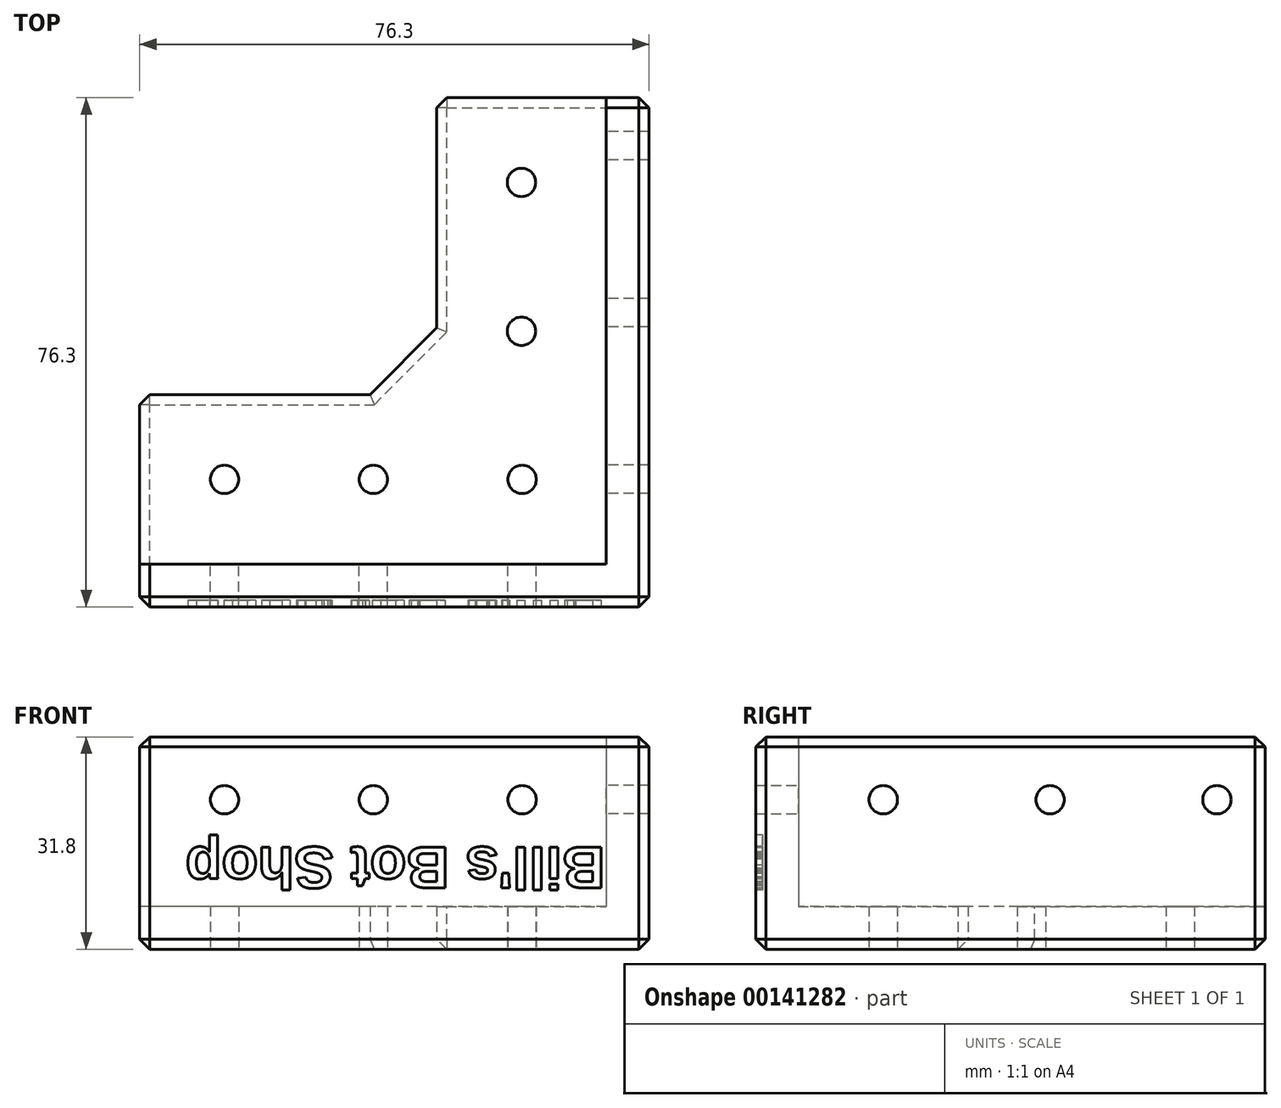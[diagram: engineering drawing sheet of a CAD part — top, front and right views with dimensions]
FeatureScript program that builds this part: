
annotation { "Feature Type Name" : "Feature", "Feature Type Description" : "" }
export const myFeature = defineFeature(function(context is Context, id is Id, definition is map)
    precondition{}
    {
        {
            var Q0;
            Q0=qCreatedBy(makeId("Top.planeOp"),FACE);
            var sketch = newSketch(context, id + "F0", { "sketchPlane" : qUnion([Q0])});
            skLineSegment(sketch, "E0.bottom", {"start": v(34.95, -12.7) * mm, "end": v(-34.95, -12.7) * mm});
            skLineSegment(sketch, "E0.top", {"start": v(34.95, 12.7) * mm, "end": v(28.55, 12.7) * mm, "construction": true});
            skLineSegment(sketch, "E0.left", {"start": v(34.95, -12.7) * mm, "end": v(34.95, 12.7) * mm});
            skLineSegment(sketch, "E0.right", {"start": v(-34.95, -12.7) * mm, "end": v(-34.95, 12.7) * mm});
            skPoint(sketch, "E0.middle", {"position": v(0, 0) * mm});
            skCircle(sketch, "E1", {"center": v(-22.25, 0) * mm, "radius": 2.12 * mm});
            skCircle(sketch, "E2.1.0.0", {"center": v(0.05, 0) * mm, "radius": 2.12 * mm});
            skCircle(sketch, "E2.2.0.0", {"center": v(22.35, 0) * mm, "radius": 2.12 * mm});
            skLineSegment(sketch, "E2.direction1", {"start": v(-22.25, 0) * mm, "end": v(0.05, 0) * mm, "construction": true});
            skLineSegment(sketch, "E3", {"start": v(28.55, 12.7) * mm, "end": v(28.55, -12.7) * mm, "construction": true});
            skLineSegment(sketch, "E4", {"start": v(9.55, 12.7) * mm, "end": v(9.55, 57.2) * mm});
            skLineSegment(sketch, "E5", {"start": v(9.55, 57.2) * mm, "end": v(34.95, 57.2) * mm});
            skLineSegment(sketch, "E6", {"start": v(34.95, 57.2) * mm, "end": v(34.95, 12.7) * mm});
            skCircle(sketch, "E7", {"center": v(22.25, 44.5) * mm, "radius": 2.12 * mm});
            skCircle(sketch, "E8", {"center": v(22.25, 22.2) * mm, "radius": 2.12 * mm});
            skLineSegment(sketch, "E9.trimOffspring", {"start": v(9.55, 12.7) * mm, "end": v(-34.95, 12.7) * mm});
            skSolve(sketch);
        }
        {
            var Q0;
            Q0=qSketchRegion(id+"F0",true);
            extrude(context, id + "F1", {"entities" : qUnion([Q0]), "depth" : 6.4 * mm});
        }
        {
            var Q0;
            Q0=makeQuery(id+"F1.opExtrude","SWEPT_FACE",FACE,{"disambiguationData":[OSD([sQuery(id+"F0.wireOp",EDGE,"E0.bottom")])]});
            var sketch = newSketch(context, id + "F2", { "sketchPlane" : qUnion([Q0])});
            skLineSegment(sketch, "E10.bottom", {"start": v(34.95, 0) * mm, "end": v(-34.95, 0) * mm});
            skLineSegment(sketch, "E10.top", {"start": v(34.95, 31.8) * mm, "end": v(-34.95, 31.8) * mm});
            skLineSegment(sketch, "E10.left", {"start": v(34.95, 0) * mm, "end": v(34.95, 31.8) * mm});
            skLineSegment(sketch, "E10.right", {"start": v(-34.95, 0) * mm, "end": v(-34.95, 31.8) * mm});
            skPoint(sketch, "E10.middle", {"position": v(0, 15.9) * mm});
            skCircle(sketch, "E11", {"center": v(-22.25, 22.4) * mm, "radius": 2.12 * mm});
            skCircle(sketch, "E12.1.0.0", {"center": v(0.05, 22.4) * mm, "radius": 2.12 * mm});
            skLineSegment(sketch, "E12.direction1", {"start": v(-22.25, 22.4) * mm, "end": v(0.05, 22.4) * mm, "construction": true});
            skLineSegment(sketch, "E13", {"start": v(28.55, 31.8) * mm, "end": v(28.55, 0) * mm, "construction": true});
            skCircle(sketch, "E14.0.2.0", {"center": v(22.35, 22.4) * mm, "radius": 2.12 * mm});
            skSolve(sketch);
        }
        {
            var Q0;
            Q0=qSketchRegion(id+"F2",true);
            extrude(context, id + "F3", {"entities" : qUnion([Q0]), "operationType" : NewBodyOperationType.ADD, "depth" : 6.4 * mm});
        }
        {
            var Q0;
            Q0=makeQuery(id+"F3.boolean.opBoolean","MERGE",FACE,{"derivedFrom":[makeQuery(id+"F1.opExtrude","SWEPT_FACE",FACE,{"disambiguationData":[OSD([sQuery(id+"F0.wireOp",EDGE,"E0.left")])]}),makeQuery(id+"F3.opExtrude","SWEPT_FACE",FACE,{"disambiguationData":[OSD([sQuery(id+"F2.wireOp",EDGE,"E10.left")])]})]});
            var sketch = newSketch(context, id + "F4", { "sketchPlane" : qUnion([Q0])});
            skLineSegment(sketch, "E15", {"start": v(-19.1, 31.8) * mm, "end": v(-19.1, 0) * mm});
            skLineSegment(sketch, "E16", {"start": v(-19.1, 0) * mm, "end": v(57.2, 0) * mm});
            skLineSegment(sketch, "E17", {"start": v(-12.7, 31.8) * mm, "end": v(-19.1, 31.8) * mm});
            skLineSegment(sketch, "E18", {"start": v(57.2, 0) * mm, "end": v(57.2, 31.8) * mm});
            skLineSegment(sketch, "E19", {"start": v(57.2, 31.8) * mm, "end": v(-12.7, 31.8) * mm});
            skCircle(sketch, "E20", {"center": v(0, 22.4) * mm, "radius": 2.12 * mm});
            skCircle(sketch, "E21.1.0.0", {"center": v(25, 22.4) * mm, "radius": 2.12 * mm});
            skCircle(sketch, "E21.2.0.0", {"center": v(50, 22.4) * mm, "radius": 2.12 * mm});
            skLineSegment(sketch, "E21.direction1", {"start": v(0, 22.4) * mm, "end": v(25, 22.4) * mm, "construction": true});
            skSolve(sketch);
        }
        {
            var Q0;
            Q0=qSketchRegion(id+"F4",true);
            extrude(context, id + "F5", {"entities" : qUnion([Q0]), "operationType" : NewBodyOperationType.ADD, "depth" : 6.4 * mm});
        }
        {
            var Q0;
            Q0=makeQuery(id+"F1.opExtrude","SWEPT_EDGE",EDGE,{"disambiguationData":[OSD([sQuery(id+"F0.wireOp",EDGE,"E4"),sQuery(id+"F0.wireOp",EDGE,"E9.trimOffspring")])]});
            chamfer(context, id + "F6", {"entities" : qUnion([Q0]), "width" : 10 * mm, "tangentPropagation" : true});
        }
        {
            var Q0;
            Q0=makeQuery(id+"F5.boolean.opBoolean","MERGE",EDGE,{"derivedFrom":[makeQuery(id+"F3.opExtrude","CAP_EDGE",EDGE,{"disambiguationData":[OSD([sQuery(id+"F2.wireOp",EDGE,"E10.bottom")])],"isStart":false}),makeQuery(id+"F5.opExtrude","SWEPT_EDGE",EDGE,{"disambiguationData":[OSD([sQuery(id+"F4.wireOp",EDGE,"E15"),sQuery(id+"F4.wireOp",EDGE,"E16")])]})]});
            var Q1;
            Q1=makeQuery(id+"F5.opExtrude","CAP_EDGE",EDGE,{"disambiguationData":[OSD([sQuery(id+"F4.wireOp",EDGE,"E16")])],"isStart":false});
            var Q2;
            Q2=makeQuery(id+"F5.opExtrude","CAP_EDGE",EDGE,{"disambiguationData":[OSD([sQuery(id+"F4.wireOp",EDGE,"E15")])],"isStart":false});
            var Q3;
            Q3=makeQuery(id+"F3.opExtrude","CAP_EDGE",EDGE,{"disambiguationData":[OSD([sQuery(id+"F2.wireOp",EDGE,"E10.right")])],"isStart":false});
            var Q4;
            Q4=makeQuery(id+"F3.boolean.opBoolean","MERGE",EDGE,{"derivedFrom":[makeQuery(id+"F1.opExtrude","CAP_EDGE",EDGE,{"disambiguationData":[OSD([sQuery(id+"F0.wireOp",EDGE,"E0.right")])],"isStart":true}),makeQuery(id+"F3.opExtrude","SWEPT_EDGE",EDGE,{"disambiguationData":[OSD([sQuery(id+"F2.wireOp",EDGE,"E10.bottom"),sQuery(id+"F2.wireOp",EDGE,"E10.right")])]})]});
            var Q5;
            Q5=makeQuery(id+"F1.opExtrude","CAP_EDGE",EDGE,{"disambiguationData":[OSD([sQuery(id+"F0.wireOp",EDGE,"E9.trimOffspring")])],"isStart":true});
            var Q6;
            Q6=makeQuery(id+"F1.opExtrude","CAP_EDGE",EDGE,{"disambiguationData":[OSD([sQuery(id+"F0.wireOp",EDGE,"E4")])],"isStart":true});
            var Q7;
            Q7=makeQuery(id+"F5.opExtrude","CAP_EDGE",EDGE,{"disambiguationData":[OSD([sQuery(id+"F4.wireOp",EDGE,"E18")])],"isStart":false});
            var Q8;
            Q8=makeQuery(id+"F5.boolean.opBoolean","MERGE",EDGE,{"derivedFrom":[makeQuery(id+"F1.opExtrude","CAP_EDGE",EDGE,{"disambiguationData":[OSD([sQuery(id+"F0.wireOp",EDGE,"E5")])],"isStart":true}),makeQuery(id+"F5.opExtrude","SWEPT_EDGE",EDGE,{"disambiguationData":[OSD([sQuery(id+"F4.wireOp",EDGE,"E16"),sQuery(id+"F4.wireOp",EDGE,"E18")])]})]});
            var Q9;
            {var subQ0=sQuery(id+"F0.wireOp",EDGE,"E9.trimOffspring");var subQ1=sQuery(id+"F0.wireOp",EDGE,"E4");Q9=makeQuery(id+"F6.opChamfer","BLEND_EDGE",EDGE,{"blendedFrom":[makeQuery(id+"F1.opExtrude","SWEPT_EDGE",EDGE,{"disambiguationData":[OSD([subQ1,subQ0])]}),makeQuery(id+"F5.boolean.opBoolean","MERGE",FACE,{"derivedFrom":[makeQuery(id+"F3.boolean.opBoolean","MERGE",FACE,{"derivedFrom":[makeQuery(id+"F1.opExtrude","CAP_FACE",FACE,{"disambiguationData":[OSD([sQuery(id+"F0.wireOp",EDGE,"E0.bottom"),sQuery(id+"F0.wireOp",EDGE,"E0.left"),sQuery(id+"F0.wireOp",EDGE,"E0.right"),sQuery(id+"F0.wireOp",EDGE,"E1"),sQuery(id+"F0.wireOp",EDGE,"E2.1.0.0"),sQuery(id+"F0.wireOp",EDGE,"E2.2.0.0"),subQ1,sQuery(id+"F0.wireOp",EDGE,"E5"),sQuery(id+"F0.wireOp",EDGE,"E6"),sQuery(id+"F0.wireOp",EDGE,"E7"),sQuery(id+"F0.wireOp",EDGE,"E8"),subQ0])],"isStart":true}),makeQuery(id+"F3.opExtrude","SWEPT_FACE",FACE,{"disambiguationData":[OSD([sQuery(id+"F2.wireOp",EDGE,"E10.bottom")])]})]}),makeQuery(id+"F5.opExtrude","SWEPT_FACE",FACE,{"disambiguationData":[OSD([sQuery(id+"F4.wireOp",EDGE,"E16")])]})]})],"blendedInto":[makeQuery(id+"F5.boolean.opBoolean","MERGE",FACE,{"derivedFrom":[makeQuery(id+"F3.boolean.opBoolean","MERGE",FACE,{"derivedFrom":[makeQuery(id+"F1.opExtrude","CAP_FACE",FACE,{"disambiguationData":[OSD([sQuery(id+"F0.wireOp",EDGE,"E0.bottom"),sQuery(id+"F0.wireOp",EDGE,"E0.left"),sQuery(id+"F0.wireOp",EDGE,"E0.right"),sQuery(id+"F0.wireOp",EDGE,"E1"),sQuery(id+"F0.wireOp",EDGE,"E2.1.0.0"),sQuery(id+"F0.wireOp",EDGE,"E2.2.0.0"),subQ1,sQuery(id+"F0.wireOp",EDGE,"E5"),sQuery(id+"F0.wireOp",EDGE,"E6"),sQuery(id+"F0.wireOp",EDGE,"E7"),sQuery(id+"F0.wireOp",EDGE,"E8"),subQ0])],"isStart":true}),makeQuery(id+"F3.opExtrude","SWEPT_FACE",FACE,{"disambiguationData":[OSD([sQuery(id+"F2.wireOp",EDGE,"E10.bottom")])]})]}),makeQuery(id+"F5.opExtrude","SWEPT_FACE",FACE,{"disambiguationData":[OSD([sQuery(id+"F4.wireOp",EDGE,"E16")])]})]})]});}
            var Q10;
            Q10=makeQuery(id+"F5.boolean.opBoolean","MERGE",EDGE,{"derivedFrom":[makeQuery(id+"F3.opExtrude","CAP_EDGE",EDGE,{"disambiguationData":[OSD([sQuery(id+"F2.wireOp",EDGE,"E10.top")])],"isStart":false}),makeQuery(id+"F5.opExtrude","SWEPT_EDGE",EDGE,{"disambiguationData":[OSD([sQuery(id+"F4.wireOp",EDGE,"E15"),sQuery(id+"F4.wireOp",EDGE,"E17")])]})]});
            var Q11;
            Q11=makeQuery(id+"F5.opExtrude","CAP_EDGE",EDGE,{"disambiguationData":[OSD([sQuery(id+"F4.wireOp",EDGE,"E17"),sQuery(id+"F4.wireOp",EDGE,"E19")])],"isStart":false});
            var Q12;
            Q12=makeQuery(id+"F1.opExtrude","SWEPT_EDGE",EDGE,{"disambiguationData":[OSD([sQuery(id+"F0.wireOp",EDGE,"E4"),sQuery(id+"F0.wireOp",EDGE,"E5")])]});
            var Q13;
            Q13=makeQuery(id+"F5.opExtrude","SWEPT_EDGE",EDGE,{"disambiguationData":[OSD([sQuery(id+"F4.wireOp",EDGE,"E18"),sQuery(id+"F4.wireOp",EDGE,"E19")])]});
            var Q14;
            Q14=makeQuery(id+"F1.opExtrude","SWEPT_EDGE",EDGE,{"disambiguationData":[OSD([sQuery(id+"F0.wireOp",EDGE,"E0.right"),sQuery(id+"F0.wireOp",EDGE,"E9.trimOffspring")])]});
            var Q15;
            Q15=makeQuery(id+"F3.opExtrude","SWEPT_EDGE",EDGE,{"disambiguationData":[OSD([sQuery(id+"F2.wireOp",EDGE,"E10.top"),sQuery(id+"F2.wireOp",EDGE,"E10.right")])]});
            chamfer(context, id + "F7", {"entities" : qUnion([Q0, Q1, Q2, Q3, Q4, Q5, Q6, Q7, Q8, Q9, Q10, Q11, Q12, Q13, Q14, Q15]), "width" : 1.5 * mm, "tangentPropagation" : true});
        }
        {
            var Q0;
            Q0=makeQuery(id+"F5.boolean.opBoolean","MERGE",FACE,{"derivedFrom":[makeQuery(id+"F3.opExtrude","CAP_FACE",FACE,{"disambiguationData":[OSD([sQuery(id+"F2.wireOp",EDGE,"E10.bottom"),sQuery(id+"F2.wireOp",EDGE,"E10.top"),sQuery(id+"F2.wireOp",EDGE,"E10.left"),sQuery(id+"F2.wireOp",EDGE,"E10.right"),sQuery(id+"F2.wireOp",EDGE,"E11"),sQuery(id+"F2.wireOp",EDGE,"E12.1.0.0"),sQuery(id+"F2.wireOp",EDGE,"E14.0.2.0")])],"isStart":false}),makeQuery(id+"F5.opExtrude","SWEPT_FACE",FACE,{"disambiguationData":[OSD([sQuery(id+"F4.wireOp",EDGE,"E15")])]})]});
            var sketch = newSketch(context, id + "F8", { "sketchPlane" : qUnion([Q0])});
            skText(sketch, "E22", { "text": "Bill\'s Bot Shop", "fontName": "Arimo-Bold.ttf"});
            const initialGuessF8  = {"E22": [0.03475, 0.0153, -1, 0, 0.0064]};
            skSetInitialGuess(sketch, initialGuessF8);
            skSolve(sketch);
        }
        {
            var Q0;
            Q0=qSketchRegion(id+"F8",true);
            extrude(context, id + "F9", {"entities" : qUnion([Q0]), "operationType" : NewBodyOperationType.REMOVE, "oppositeDirection" : true, "depth" : 1 * mm});
        }
    });
